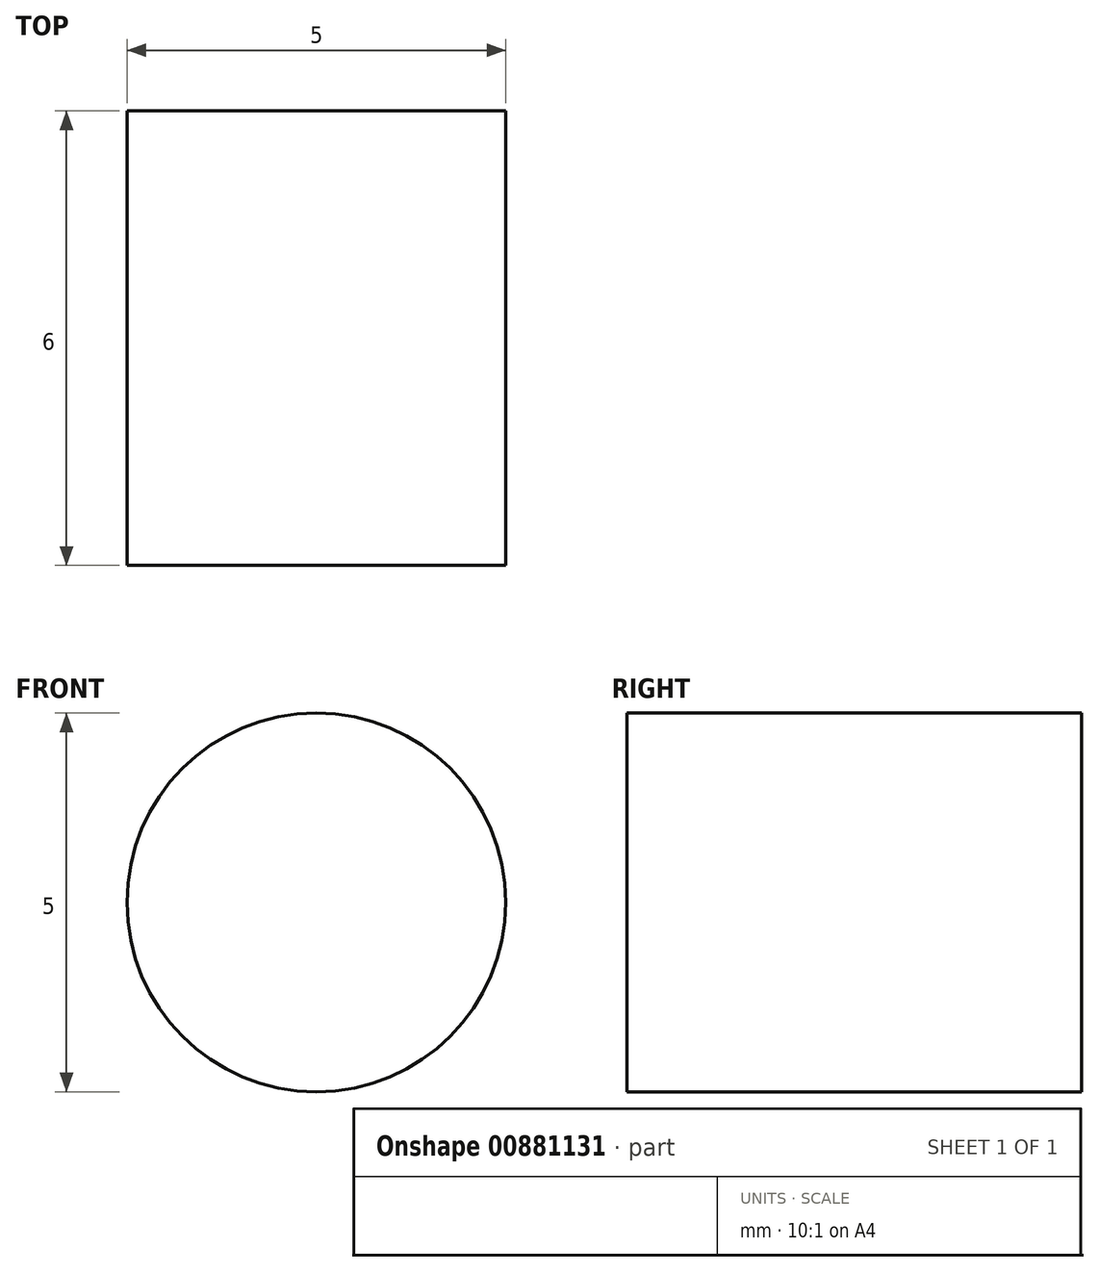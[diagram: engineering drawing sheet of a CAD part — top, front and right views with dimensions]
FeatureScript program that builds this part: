
annotation { "Feature Type Name" : "Feature", "Feature Type Description" : "" }
export const myFeature = defineFeature(function(context is Context, id is Id, definition is map)
    precondition{}
    {
        {
            var Q0;
            Q0=qCreatedBy(makeId("Front.planeOp"),FACE);
            var sketch = newSketch(context, id + "F0", { "sketchPlane" : qUnion([Q0])});
            skCircle(sketch, "E0", {"center": v(-0.61, 0) * mm, "radius": 2.5 * mm});
            skSolve(sketch);
        }
        {
            var Q0;
            Q0=makeQuery(id+"F0.imprint","IMPRINT",FACE,{"disambiguationData":[TD([[makeQuery(id+"F0.imprint","IMPRINT",EDGE,{"derivedFrom":sQuery(id+"F0.wireOp",EDGE,"E0")}),1.0]])]});
            extrude(context, id + "F1", {"entities" : qUnion([Q0]), "depth" : 6 * mm, "offsetDistance" : 25 * mm});
        }
    });
